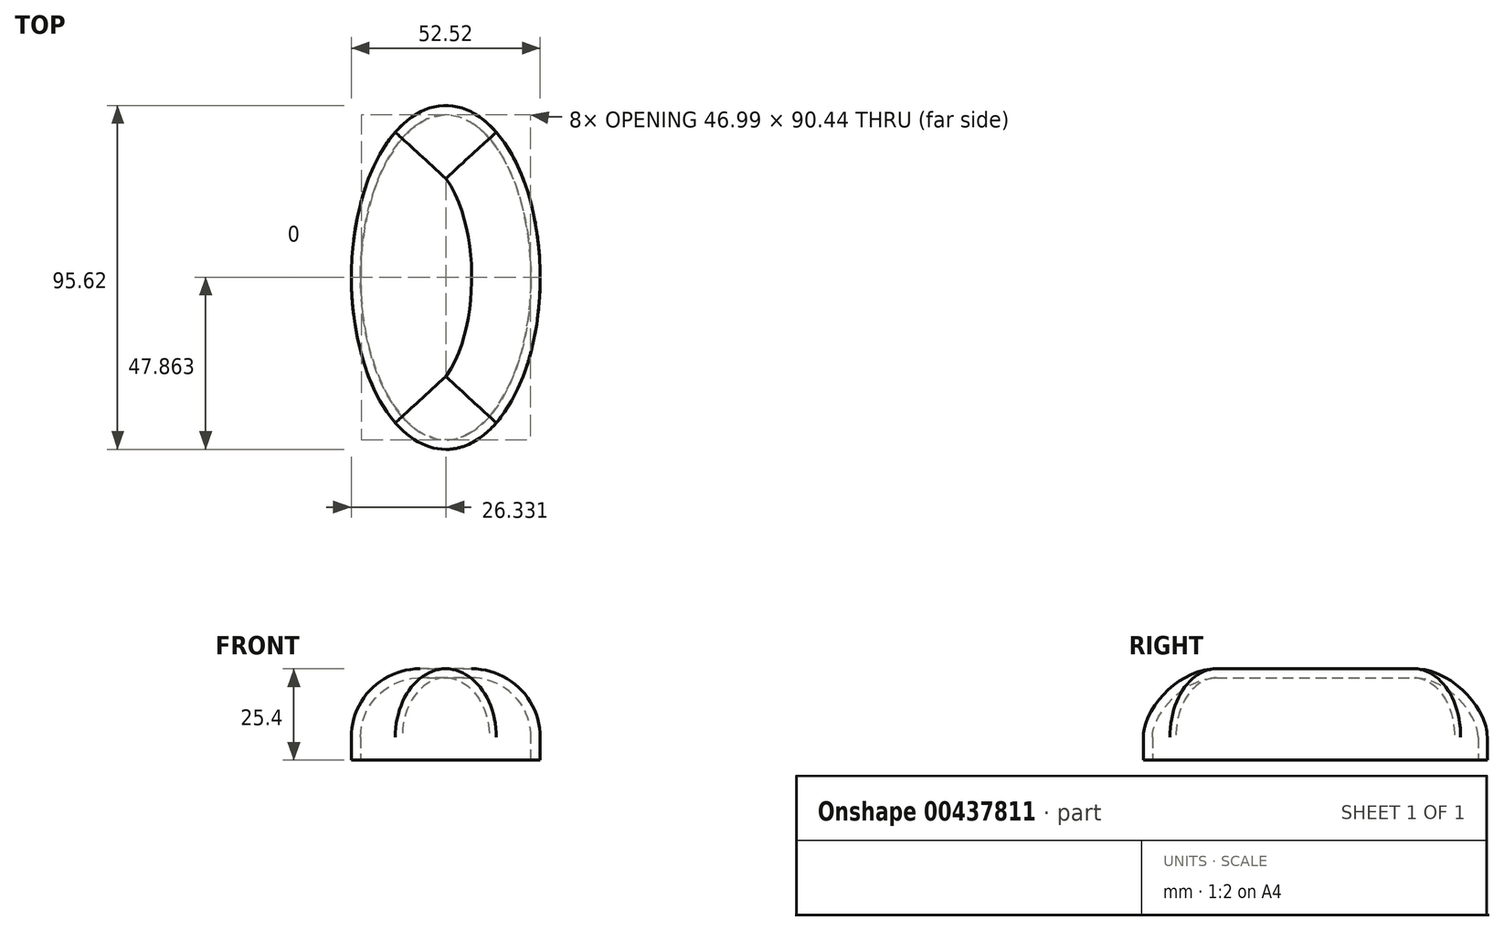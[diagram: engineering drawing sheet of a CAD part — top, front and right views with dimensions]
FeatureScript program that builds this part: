
annotation { "Feature Type Name" : "Feature", "Feature Type Description" : "" }
export const myFeature = defineFeature(function(context is Context, id is Id, definition is map)
    precondition{}
    {
        {
            var Q0;
            Q0=qCreatedBy(makeId("Top.planeOp"),FACE);
            var sketch = newSketch(context, id + "F0", { "sketchPlane" : qUnion([Q0])});
            skEllipse(sketch, "E0", {"center": v(0, 0) * mm, "majorRadius": 47.81 * mm, "minorRadius": 26.26 * mm, "majorAxis": v(0, -1)});
            skSolve(sketch);
        }
        {
            var Q0;
            Q0=makeQuery(id+"F0.imprint","IMPRINT",FACE,{"disambiguationData":[TD([[makeQuery(id+"F0.imprint","IMPRINT",EDGE,{"derivedFrom":sQuery(id+"F0.wireOp",EDGE,"E0")}),1.0]])]});
            extrude(context, id + "F1", {"entities" : qUnion([Q0]), "depth" : 25.4 * mm});
        }
        {
            var Q0;
            Q0=makeQuery(id+"F1.opExtrude","CAP_FACE",FACE,{"disambiguationData":[OSD([sQuery(id+"F0.wireOp",EDGE,"E0")])],"isStart":false});
            fillet(context, id + "F2", {"entities" : qUnion([Q0]), "radius" : 19.05 * mm, "tangentPropagation" : true, "allowEdgeOverflow" : false});
        }
        {
            var Q0;
            Q0=makeQuery(id+"F1.opExtrude","CAP_FACE",FACE,{"disambiguationData":[OSD([sQuery(id+"F0.wireOp",EDGE,"E0")])],"isStart":true});
            shell(context, id + "F3", {"entities" : qUnion([Q0]), "thickness" : 2.54 * mm});
        }
    });
